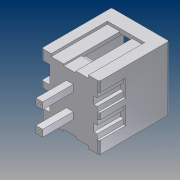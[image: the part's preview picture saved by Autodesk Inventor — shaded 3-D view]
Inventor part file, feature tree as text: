
AUTODESK INVENTOR PART (.ipt)
format: ipt  version: unknown  size: 301,568 bytes
history: native  units: mm (DEFAULTED — no unit token found)
features: extrude x15, sketch x15, pattern_linear x4
ambient origin geometry x8: Origin, YZ Plane, XZ Plane, XY Plane, X Axis, Y Axis, Z Axis, Center Point
feature tree (34):
  extrude  "Extrusion1"  Depth=7.5mm TaperAngle=0.0deg
  extrude  "Extrusion2"  Depth=7.7mm TaperAngle=0.0deg
  extrude  "Extrusion3"  Depth=6.0mm TaperAngle=0.0deg
  extrude  "Extrusion4"  Depth=20.0mm TaperAngle=0.0deg
  extrude  "Extrusion5"  Depth=20.0mm TaperAngle=0.0deg
  extrude  "Extrusion6"  Depth=20.0mm TaperAngle=0.0deg
  extrude  "Extrusion7"  Depth=8.3mm TaperAngle=0.0deg
  pattern_linear  "Rectangular Pattern1"  Count1=2 Spacing1=3.5mm
  extrude  "Extrusion8"  Depth=3.9mm TaperAngle=0.0deg
  pattern_linear  "Rectangular Pattern2"  [2 undecoded]
  extrude  "Extrusion9"  [1 undecoded]
  pattern_linear  "Rectangular Pattern3"  [2 undecoded]
  extrude  "Extrusion10"  [1 undecoded]
  extrude  "Extrusion11"  [1 undecoded]
  extrude  "Extrusion12"  [1 undecoded]
  pattern_linear  "Rectangular Pattern4"  [2 undecoded]
  extrude  "Extrusion13"  [1 undecoded]
  extrude  "Extrusion14"  [1 undecoded]
  extrude  "Extrusion15"  [1 undecoded]
  sketch  "Skizze_1"  dims[d0=9.4mm d1=0.0mm d2=7.5mm d3=0.0mm]
  sketch  "Skizze_2"  dims[d4=7.7mm d5=0.0mm d6=7.7mm d7=0.0mm]
  sketch  "Skizze_3"  dims[d8=6.0mm d9=0.0mm d10=6.0mm d11=0.0mm]
  sketch  "Skizze_4"  dims[d12=3.6mm d13=0.0mm d14=20.0mm d16=3.5mm d17=10.0mm d19=0.0mm]
  sketch  "Skizze_5"  dims[d20=9.3mm d21=0.0mm d22=20.0mm d24=3.5mm d25=10.0mm d27=0.0mm]
  sketch  "Skizze_6"  dims[d28=4.5mm d29=0.0mm d30=20.0mm d32=3.5mm d33=10.0mm d35=0.0mm]
  sketch  "Skizze_7"  dims[d36=8.3mm d37=0.0mm d38=8.3mm d39=0.0mm]
  sketch  "Skizze_9"  dims[d40=9.15mm d41=0.0mm d42=20.0mm d44=3.5mm d45=10.0mm d47=0.0mm]
  sketch  "Skizze_11"  dims[d48=3.9mm d49=0.0mm d50=3.9mm d51=0.0mm]
  sketch  "Skizze_13"  dims[d52=0.254mm]
  sketch  "Skizze_14"  dims[d53=0.254mm d54=0.0mm]
  sketch  "Skizze_15"
  sketch  "Skizze_17"
  sketch  "Skizze_18"
  sketch  "Sketch15"
note: 13 required parameter values undecoded (feature->parameter linkage not recoverable at this tier; creation-order binding heuristic only, values carry confidence <= 0.55)
